# Revit family: STL21121_27_30_40_50
name_source: partatom
category: Luminárias
units: mm (PartAtom-declared; Revit-internal decimal feet)

## family parameters
Com base no plano de trabalho = Não
Compartilhado = Não
Corte com vazios quando carregada = Não
Cota do conector redondo = Utilizar diâmetro
Fonte luminosa = Sim
Manter orientação da anotação = Não
Ponto de cálculo do ambiente = Não
Sempre na vertical = Sim
Tipo de parte = Normal

## types (4) — shared parameters
Comprimento = 0.02 m
Cromado = Cromado
Dimerização = Não dimerizável
Estrutura = Al - Branco
Fabricante = Stella
Filtro de cor = 16777215
Grau de proteção (IP) = IP20
IRC (Índice de reprodução de cores) = >80
Largura = 0.01 m
Modelo = Bipino G9
Potência = 2 W
Tensão Elétrica = 127V
Troca de temperatura da cor de lâmpada com esmaecimento = <Nenhum>
URL = https://stella.com.br
Ângulo de Abertura = 280º
Ângulo de inclinação = 90.00°
zero-valued in all types: Elevação padrão

## per-type parameters (varying)
| type | Arquivo de rede fotométrica | LED |
| STL21121/27 - 127V | STELLA - STL21121-27 - BIPINO G9 1,7W .ies | Luminoso - 2700K |
| STL21121/30 - 127V | STELLA - STL21121-30 - BIPINO G9 1,7W .ies | Luminoso - 3000K |
| STL21121/40 - 127V | STELLA - STL21121-40 - BIPINO G9 1,7W .ies | Luminoso - 4000K |
| STL21121/50 - 127V | STELLA - STL21121-50 - BIPINO G9 1,7W.ies | Luminoso - 5000K |
